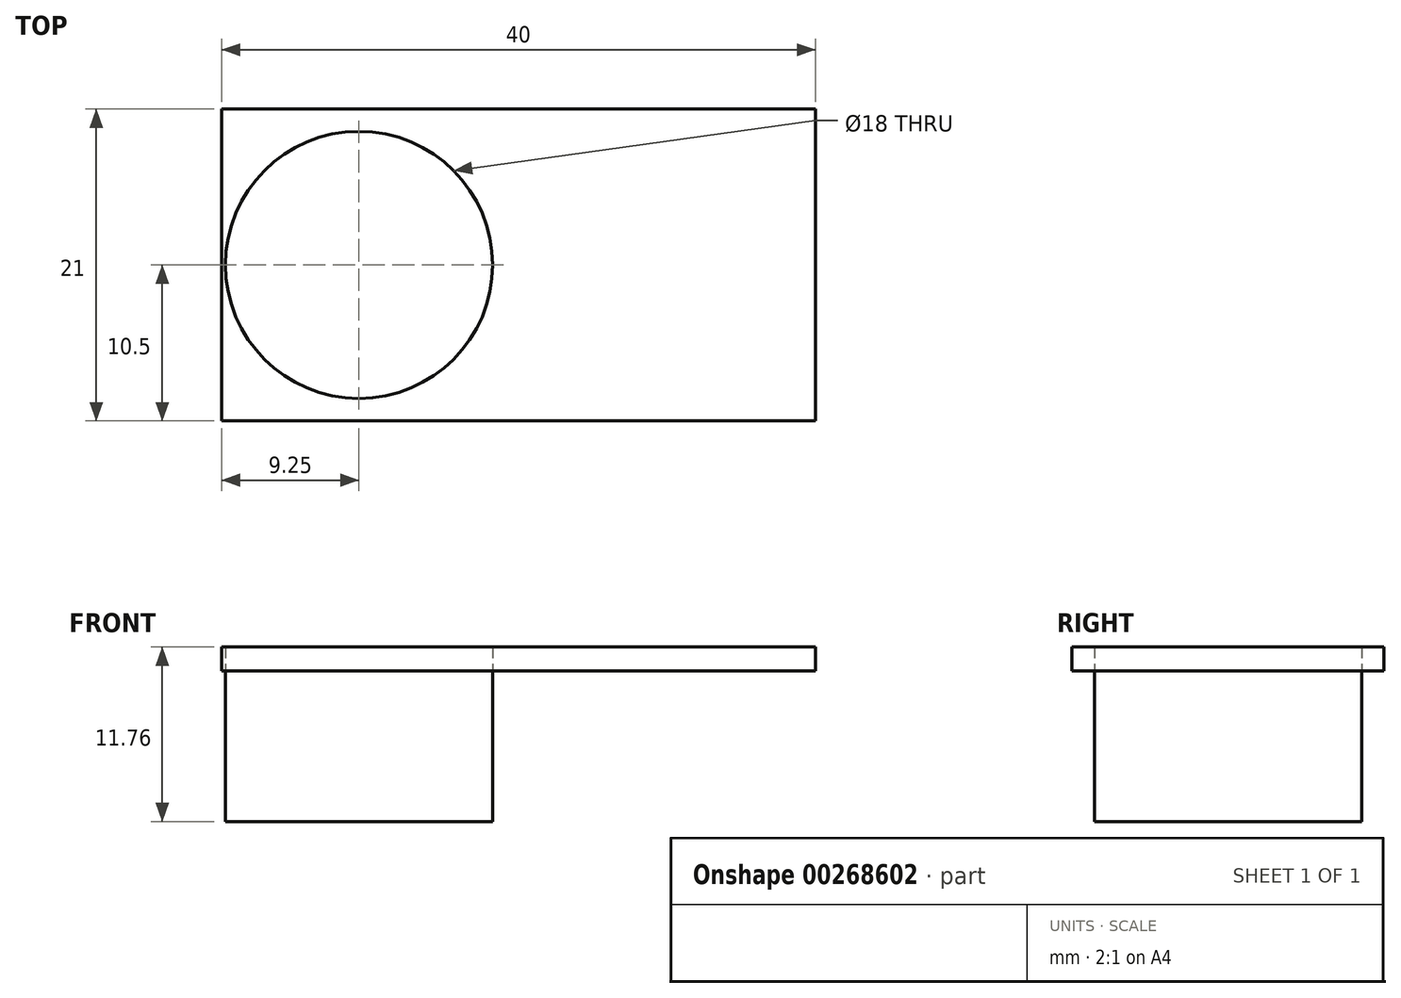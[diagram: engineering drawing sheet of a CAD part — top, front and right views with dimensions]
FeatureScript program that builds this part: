
annotation { "Feature Type Name" : "Feature", "Feature Type Description" : "" }
export const myFeature = defineFeature(function(context is Context, id is Id, definition is map)
    precondition{}
    {
        {
            var Q0;
            Q0=qCreatedBy(makeId("Top.planeOp"),FACE);
            var sketch = newSketch(context, id + "F0", { "sketchPlane" : qUnion([Q0])});
            skCircle(sketch, "E0", {"center": v(0, 0) * mm, "radius": 9 * mm});
            skSolve(sketch);
        }
        {
            var Q0;
            Q0 = qSketchRegion(id + "F0", true);
            extrude(context, id + "F1", {"entities" : qUnion([Q0]), "depth" : 10.16 * mm, "offsetDistance" : 25.4 * mm});
        }
        {
            var Q0;
            Q0=makeQuery(id+"F1.opExtrude","CAP_FACE",FACE,{"disambiguationData":[OSD([sQuery(id+"F0.wireOp",EDGE,"E0")])],"isStart":false});
            var sketch = newSketch(context, id + "F2", { "sketchPlane" : qUnion([Q0])});
            skLineSegment(sketch, "E1.bottom", {"start": v(-9.25, 10.5) * mm, "end": v(30.75, 10.5) * mm});
            skLineSegment(sketch, "E1.top", {"start": v(-9.25, -10.5) * mm, "end": v(30.75, -10.5) * mm});
            skLineSegment(sketch, "E1.left", {"start": v(-9.25, 10.5) * mm, "end": v(-9.25, -10.5) * mm});
            skLineSegment(sketch, "E1.right", {"start": v(30.75, 10.5) * mm, "end": v(30.75, -10.5) * mm});
            skSolve(sketch);
        }
        {
            var Q0;
            {var subQ4=sQuery(id+"F2.wireOp",EDGE,"E1.bottom");Q0=makeQuery(id+"F2.imprint","IMPRINT",FACE,{"disambiguationData":[TD([[makeQuery(id+"F2.imprint","IMPRINT",EDGE,{"derivedFrom":subQ4}),-1.0]])]});}
            extrude(context, id + "F3", {"entities" : qUnion([Q0]), "depth" : 1.6 * mm, "offsetDistance" : 25.4 * mm});
        }
    });
